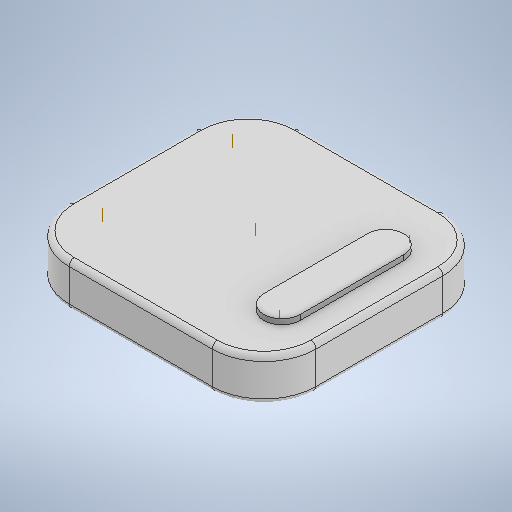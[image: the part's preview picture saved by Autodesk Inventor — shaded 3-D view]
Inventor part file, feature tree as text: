
AUTODESK INVENTOR PART (.ipt)
format: ipt  version: 2025 (Build 290162000, 162)  size: 288,256 bytes
history: native  units: mm
features: sketch x4, other x4, extrude x3, fillet x1
ambient origin geometry x8: Origin, YZ Plane, XZ Plane, XY Plane, X Axis, Y Axis, Z Axis, Center Point
bodies: Solid1 (feature_tree)
feature tree (12):
  extrude  "Extrusion1"  Depth=44.5mm
  fillet  "Fillet1"  Radius=10.0mm
  sketch  "Sketch2"  dims[d4=8.25mm d5=0.0mm d6=1.0mm]
  other  "Work Axis1"
  other  "Work Axis2"
  other  "Work Axis3"
  other  "Work Axis4"
  extrude  "Extrusion2"  Depth=1.0mm
  extrude  "Extrusion4"  Depth=34.0mm
  sketch  "Sketch1"  dims[d0=47.6mm d1=44.5mm d3=10.0mm]
  sketch  "Sketch3"  dims[d7=25.0mm d8=34.0mm]
  sketch  "Sketch5"  dims[d9=5.0mm d10=1.25mm d11=135.0deg d12=0.5mm d13=0.0mm d16=10.0mm d17=7.0mm d18=15.0mm d19=1.0mm d20=0.0mm]
